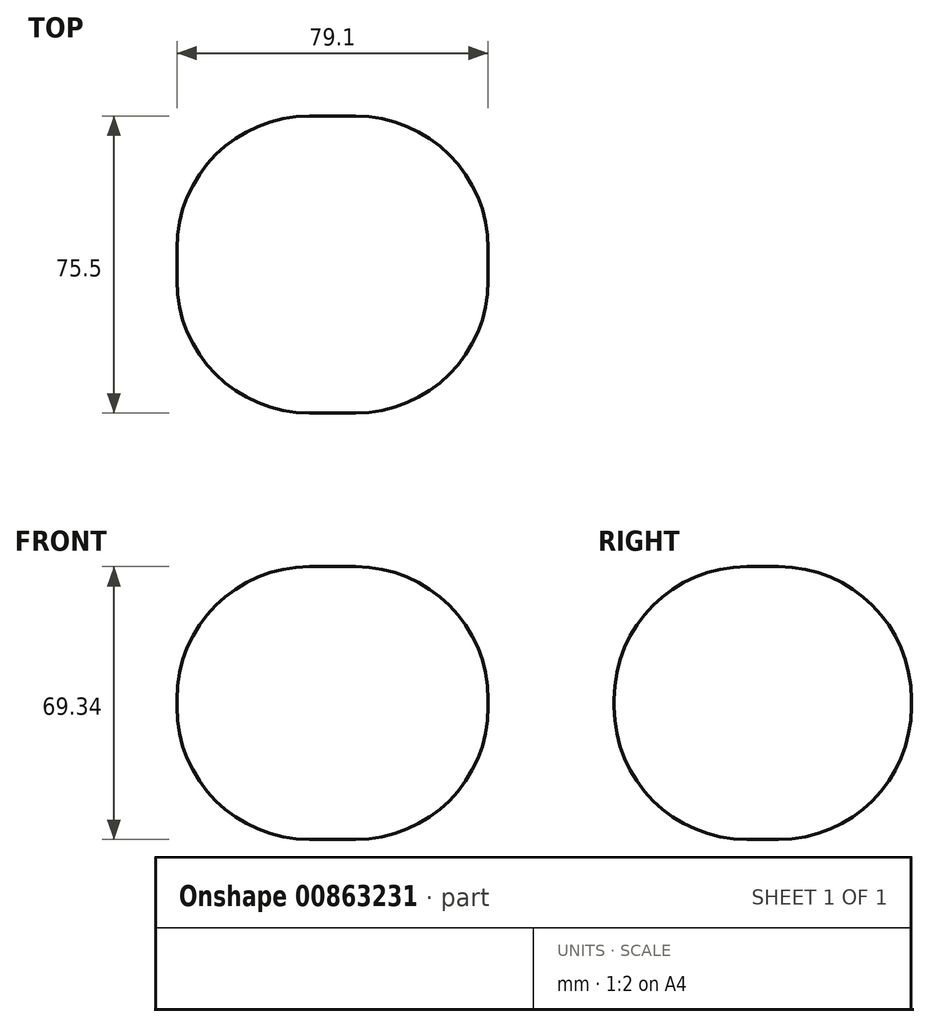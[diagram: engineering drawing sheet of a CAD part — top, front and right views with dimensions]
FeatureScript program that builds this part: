
annotation { "Feature Type Name" : "Feature", "Feature Type Description" : "" }
export const myFeature = defineFeature(function(context is Context, id is Id, definition is map)
    precondition{}
    {
        {
            var Q0;
            Q0=qCreatedBy(makeId("Top.planeOp"),FACE);
            var sketch = newSketch(context, id + "F0", { "sketchPlane" : qUnion([Q0])});
            skLineSegment(sketch, "E0.bottom", {"start": v(39.55, 37.75) * mm, "end": v(-39.55, 37.75) * mm});
            skLineSegment(sketch, "E0.top", {"start": v(39.55, -37.75) * mm, "end": v(-39.55, -37.75) * mm});
            skLineSegment(sketch, "E0.left", {"start": v(39.55, 37.75) * mm, "end": v(39.55, -37.75) * mm});
            skLineSegment(sketch, "E0.right", {"start": v(-39.55, 37.75) * mm, "end": v(-39.55, -37.75) * mm});
            skPoint(sketch, "E0.middle", {"position": v(0, 0) * mm});
            skCircle(sketch, "E1", {"center": v(0, 0) * mm, "radius": 17.85 * mm});
            skSolve(sketch);
        }
        {
            var Q0;
            Q0 = qSketchRegion(id + "F0", true);
            var Q1;
            Q1=makeQuery(id+"F0.imprint","IMPRINT",FACE,{"disambiguationData":[TD([[makeQuery(id+"F0.imprint","IMPRINT",EDGE,{"derivedFrom":sQuery(id+"F0.wireOp",EDGE,"E1")}),1.0]])]});
            extrude(context, id + "F1", {"entities" : qUnion([Q0, Q1]), "depth" : 69.34 * mm, "offsetDistance" : 25.4 * mm});
        }
        {
            var Q0;
            Q0=makeQuery(id+"F1.opExtrude","CAP_EDGE",EDGE,{"disambiguationData":[OSD([sQuery(id+"F0.wireOp",EDGE,"E0.left")])],"isStart":false});
            var Q1;
            Q1=makeQuery(id+"F1.opExtrude","CAP_EDGE",EDGE,{"disambiguationData":[OSD([sQuery(id+"F0.wireOp",EDGE,"E0.top")])],"isStart":false});
            var Q2;
            Q2=makeQuery(id+"F1.opExtrude","SWEPT_FACE",FACE,{"disambiguationData":[OSD([sQuery(id+"F0.wireOp",EDGE,"E0.right")])]});
            var Q3;
            Q3=makeQuery(id+"F1.opExtrude","SWEPT_FACE",FACE,{"disambiguationData":[OSD([sQuery(id+"F0.wireOp",EDGE,"E0.left")])]});
            var Q4;
            Q4=makeQuery(id+"F1.opExtrude","SWEPT_FACE",FACE,{"disambiguationData":[OSD([sQuery(id+"F0.wireOp",EDGE,"E0.top")])]});
            var Q5;
            Q5=makeQuery(id+"F1.opExtrude","SWEPT_FACE",FACE,{"disambiguationData":[OSD([sQuery(id+"F0.wireOp",EDGE,"E0.bottom")])]});
            fillet(context, id + "F2", {"entities" : qUnion([Q0, Q1, Q2, Q3, Q4, Q5]), "radius" : 33.73 * mm, "tangentPropagation" : true, "allowEdgeOverflow" : false});
        }
    });
